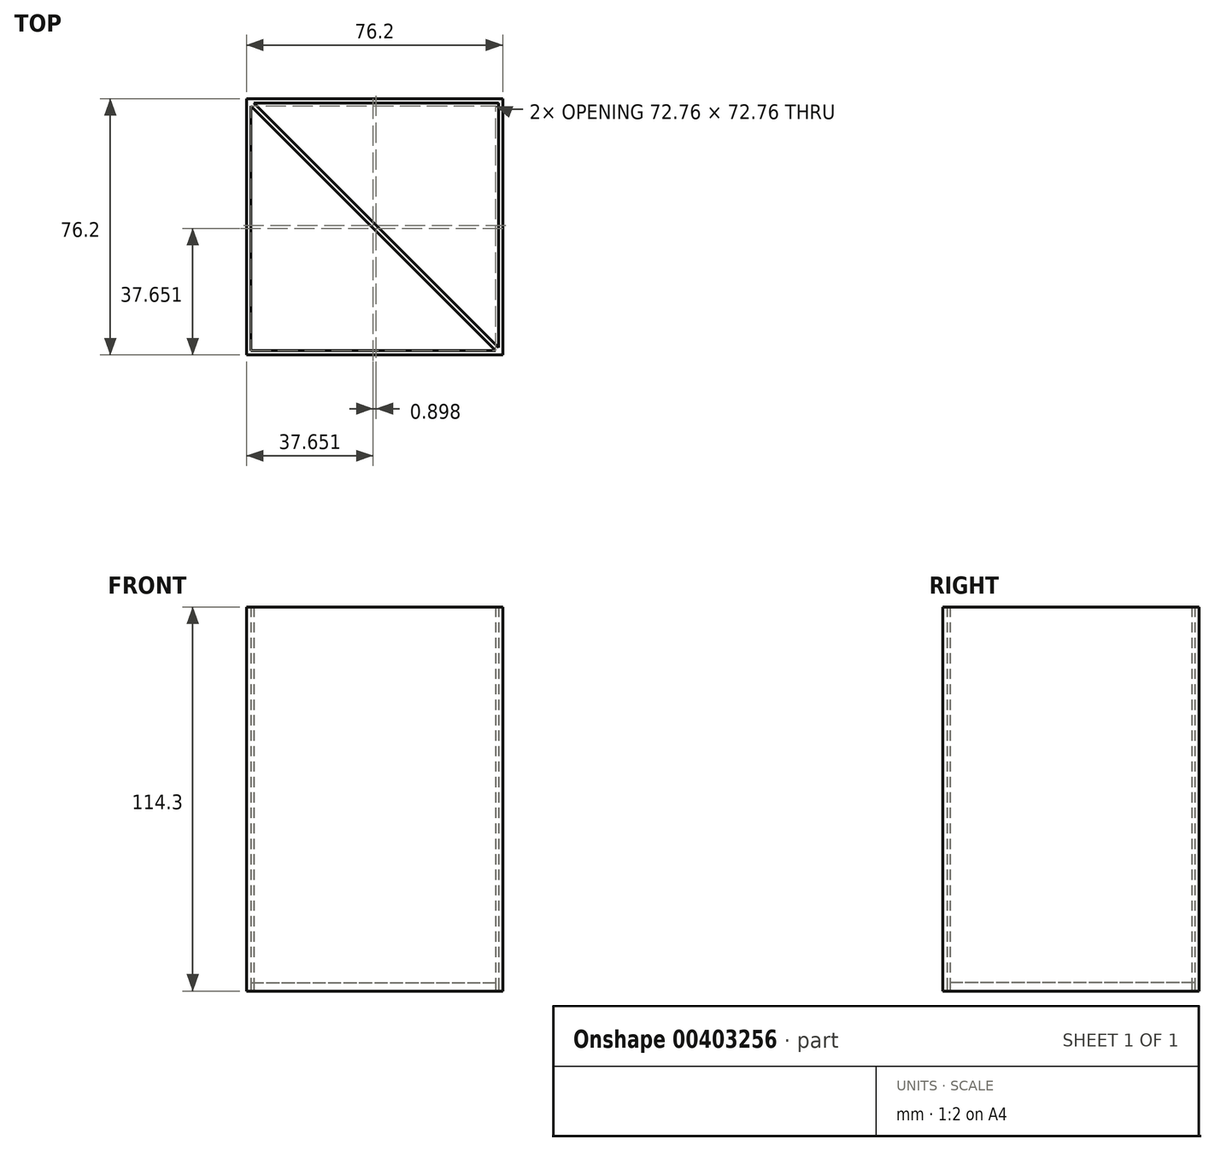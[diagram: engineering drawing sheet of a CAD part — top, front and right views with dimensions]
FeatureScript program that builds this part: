
annotation { "Feature Type Name" : "Feature", "Feature Type Description" : "" }
export const myFeature = defineFeature(function(context is Context, id is Id, definition is map)
    precondition{}
    {
        {
            var Q0;
            Q0=qCreatedBy(makeId("Top.planeOp"),FACE);
            var sketch = newSketch(context, id + "F0", { "sketchPlane" : qUnion([Q0])});
            skLineSegment(sketch, "E0.bottom", {"start": v(-38.1, 38.1) * mm, "end": v(38.1, 38.1) * mm});
            skLineSegment(sketch, "E0.top", {"start": v(-38.1, -38.1) * mm, "end": v(38.1, -38.1) * mm});
            skLineSegment(sketch, "E0.left", {"start": v(-38.1, 38.1) * mm, "end": v(-38.1, -38.1) * mm});
            skLineSegment(sketch, "E0.right", {"start": v(38.1, 38.1) * mm, "end": v(38.1, -38.1) * mm});
            skPoint(sketch, "E0.middle", {"position": v(0, 0) * mm});
            skLineSegment(sketch, "E1.bottom", {"start": v(-36.83, 36.83) * mm, "end": v(36.83, 36.83) * mm});
            skLineSegment(sketch, "E1.top", {"start": v(-36.83, -36.83) * mm, "end": v(36.83, -36.83) * mm});
            skLineSegment(sketch, "E1.left", {"start": v(-36.83, 36.83) * mm, "end": v(-36.83, -36.83) * mm});
            skLineSegment(sketch, "E1.right", {"start": v(36.83, 36.83) * mm, "end": v(36.83, -36.83) * mm});
            skCircle(sketch, "E2", {"center": v(-38.1, 38.1) * mm, "radius": 0.64 * mm});
            skCircle(sketch, "E3", {"center": v(38.1, -38.1) * mm, "radius": 0.64 * mm});
            skLineSegment(sketch, "E4", {"start": v(-41.25, 40.35) * mm, "end": v(41.25, -42.15) * mm});
            skLineSegment(sketch, "E5", {"start": v(-40.97, 41.87) * mm, "end": v(42.15, -41.25) * mm});
            skSolve(sketch);
        }
        {
            var Q0;
            {var subQ0=sQuery(id+"F0.wireOp",EDGE,"E1.left");var subQ1=sQuery(id+"F0.wireOp",EDGE,"E1.top");var subQ2=makeQuery(id+"F0.imprint","INTERSECT",VERTEX,{"derivedFrom":[subQ1,subQ0]});Q0=makeQuery(id+"F0.imprint","IMPRINT",FACE,{"disambiguationData":[TD([[makeQuery(id+"F0.imprint","IMPRINT",EDGE,{"disambiguationData":[TD([[subQ2,-1.0]])],"derivedFrom":subQ1}),1.0]])]});}
            var Q1;
            {var subQ0=sQuery(id+"F0.wireOp",EDGE,"E1.right");var subQ1=sQuery(id+"F0.wireOp",EDGE,"E1.bottom");var subQ2=makeQuery(id+"F0.imprint","INTERSECT",VERTEX,{"derivedFrom":[subQ1,subQ0]});Q1=makeQuery(id+"F0.imprint","IMPRINT",FACE,{"disambiguationData":[TD([[makeQuery(id+"F0.imprint","IMPRINT",EDGE,{"disambiguationData":[TD([[subQ2,1.0]])],"derivedFrom":subQ1}),-1.0]])]});}
            extrude(context, id + "F1", {"entities" : qUnion([Q0, Q1]), "depth" : 2.54 * mm});
        }
        {
            var Q0;
            {var subQ0=sQuery(id+"F0.wireOp",EDGE,"E0.left");var subQ1=sQuery(id+"F0.wireOp",EDGE,"E0.bottom");var subQ2=makeQuery(id+"F0.imprint","INTERSECT",VERTEX,{"derivedFrom":[subQ1,subQ0]});Q0=makeQuery(id+"F0.imprint","IMPRINT",FACE,{"disambiguationData":[TD([[makeQuery(id+"F0.imprint","IMPRINT",EDGE,{"disambiguationData":[TD([[subQ2,-1.0]])],"derivedFrom":subQ1}),-1.0]])]});}
            var Q1;
            {var subQ3=sQuery(id+"F0.wireOp",EDGE,"E5");var subQ5=sQuery(id+"F0.wireOp",EDGE,"E0.bottom");var subQ6=makeQuery(id+"F0.imprint","INTERSECT",VERTEX,{"derivedFrom":[subQ5,subQ3]});Q1=makeQuery(id+"F0.imprint","IMPRINT",FACE,{"disambiguationData":[TD([[makeQuery(id+"F0.imprint","IMPRINT",EDGE,{"disambiguationData":[TD([[subQ6,1.0]])],"derivedFrom":subQ5}),-1.0]])]});}
            var Q2;
            {var subQ6=sQuery(id+"F0.wireOp",EDGE,"E0.left");var subQ7=sQuery(id+"F0.wireOp",EDGE,"E0.top");var subQ8=makeQuery(id+"F0.imprint","INTERSECT",VERTEX,{"derivedFrom":[subQ7,subQ6]});Q2=makeQuery(id+"F0.imprint","IMPRINT",FACE,{"disambiguationData":[TD([[makeQuery(id+"F0.imprint","IMPRINT",EDGE,{"disambiguationData":[TD([[subQ8,-1.0]])],"derivedFrom":subQ7}),1.0]])]});}
            var Q3;
            {var subQ7=sQuery(id+"F0.wireOp",EDGE,"E1.left");var subQ9=sQuery(id+"F0.wireOp",EDGE,"E1.bottom");var subQ10=makeQuery(id+"F0.imprint","INTERSECT",VERTEX,{"derivedFrom":[subQ9,subQ7]});Q3=makeQuery(id+"F0.imprint","IMPRINT",FACE,{"disambiguationData":[TD([[makeQuery(id+"F0.imprint","IMPRINT",EDGE,{"disambiguationData":[TD([[subQ10,-1.0]])],"derivedFrom":subQ9}),-1.0]])]});}
            var Q4;
            {var subQ6=sQuery(id+"F0.wireOp",EDGE,"E0.right");var subQ7=sQuery(id+"F0.wireOp",EDGE,"E0.bottom");var subQ8=makeQuery(id+"F0.imprint","INTERSECT",VERTEX,{"derivedFrom":[subQ7,subQ6]});Q4=makeQuery(id+"F0.imprint","IMPRINT",FACE,{"disambiguationData":[TD([[makeQuery(id+"F0.imprint","IMPRINT",EDGE,{"disambiguationData":[TD([[subQ8,1.0]])],"derivedFrom":subQ7}),-1.0]])]});}
            var Q5;
            {var subQ3=sQuery(id+"F0.wireOp",EDGE,"E4");var subQ5=sQuery(id+"F0.wireOp",EDGE,"E0.top");var subQ6=makeQuery(id+"F0.imprint","INTERSECT",VERTEX,{"derivedFrom":[subQ5,subQ3]});Q5=makeQuery(id+"F0.imprint","IMPRINT",FACE,{"disambiguationData":[TD([[makeQuery(id+"F0.imprint","IMPRINT",EDGE,{"disambiguationData":[TD([[subQ6,-1.0]])],"derivedFrom":subQ5}),1.0]])]});}
            var Q6;
            {var subQ0=sQuery(id+"F0.wireOp",EDGE,"E0.right");var subQ1=sQuery(id+"F0.wireOp",EDGE,"E0.top");var subQ2=makeQuery(id+"F0.imprint","INTERSECT",VERTEX,{"derivedFrom":[subQ1,subQ0]});Q6=makeQuery(id+"F0.imprint","IMPRINT",FACE,{"disambiguationData":[TD([[makeQuery(id+"F0.imprint","IMPRINT",EDGE,{"disambiguationData":[TD([[subQ2,1.0]])],"derivedFrom":subQ1}),1.0]])]});}
            extrude(context, id + "F2", {"entities" : qUnion([Q0, Q1, Q2, Q3, Q4, Q5, Q6]), "depth" : 114.3 * mm});
        }
    });
